# Revit family: 546910001_Cepillera de Vaso Nilo
name_source: partatom
category: Plumbing Fixtures
units: mm (PartAtom-declared; Revit-internal decimal feet)

## family parameters
Always vertical = Yes
Cut with Voids When Loaded = No
Host = Wall
OmniClass Number = 23.19.25.13.21.17
OmniClass Title = Fittings
Part Type = Normal
Room Calculation Point = No
Round Connector Dimension = Use Diameter
Shared = No

## types (1)
- Nilo
    Acabado = Corona_Plastico_Blanco
    Alto = 600 mm
    Ancho = 132 mm
    Creado por = IDD
    Description = • Los accesorios de baño Nilo, diseño robusto y funcional.
• Acabado superior, mayor espesor en el cromado que lo hace más
brillante y resistente a la corrosión.
• Fácil limpieza: Diseño que evita la acumulación de impurezas.
• Resistencia a cargas o peso máximo de 9 kg. (19,8 lb.).
• El toallero barra tiene una resistencia de 23 Kg. (50.7 lb).
    Fecha de creación = 13/08/2020
    Garantía = 5 Años (Grival)
    Garantía Acabados = 2 Años (Cromado)
    Longitud = 94 mm
    Manufacturer = Corona
    Material = Corona_Cromado
    Peso Bruto aprox = 602 gr. 1,33 lb.
    Peso Neto aprox = 471 gr. 1,038 lb.
    Resistencia a cargas o peso máximo = 9 kg. (19,8 lb.).
    URL = https://www.grival.com

## geometry (parser evidence)
native form markers: Sweep x4
no freeform markers — native parametric forms only
